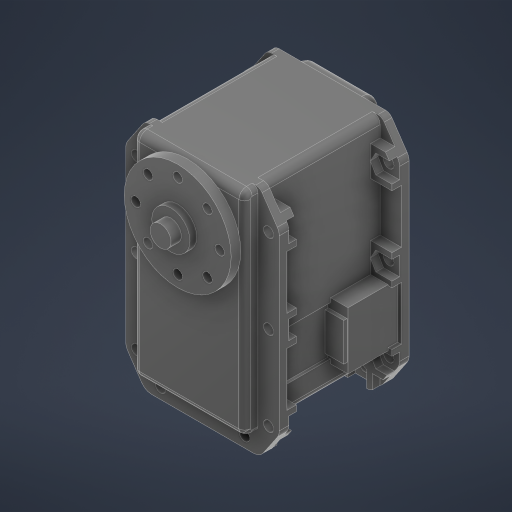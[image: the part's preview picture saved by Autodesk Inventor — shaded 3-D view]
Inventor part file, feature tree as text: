
AUTODESK INVENTOR PART (.ipt)
format: ipt  version: 2024 (Build 280153000, 153)  size: 668,160 bytes
history: native  units: mm
features: other x5, extrude x1, projected_geometry x1
ambient origin geometry x8: Origin, YZ Plane, XZ Plane, XY Plane, X Axis, Y Axis, Z Axis, Center Point
bodies: Body1 (feature_tree)
feature tree (7):
  other  "솔리드1"
  extrude  "돌출1"  Depth=22.0mm
  other  "작업 평면1"
  other  "작업 평면2"
  other  "작업 평면3"
  projected_geometry  "투영된 루프1"
  other  "기준1"
